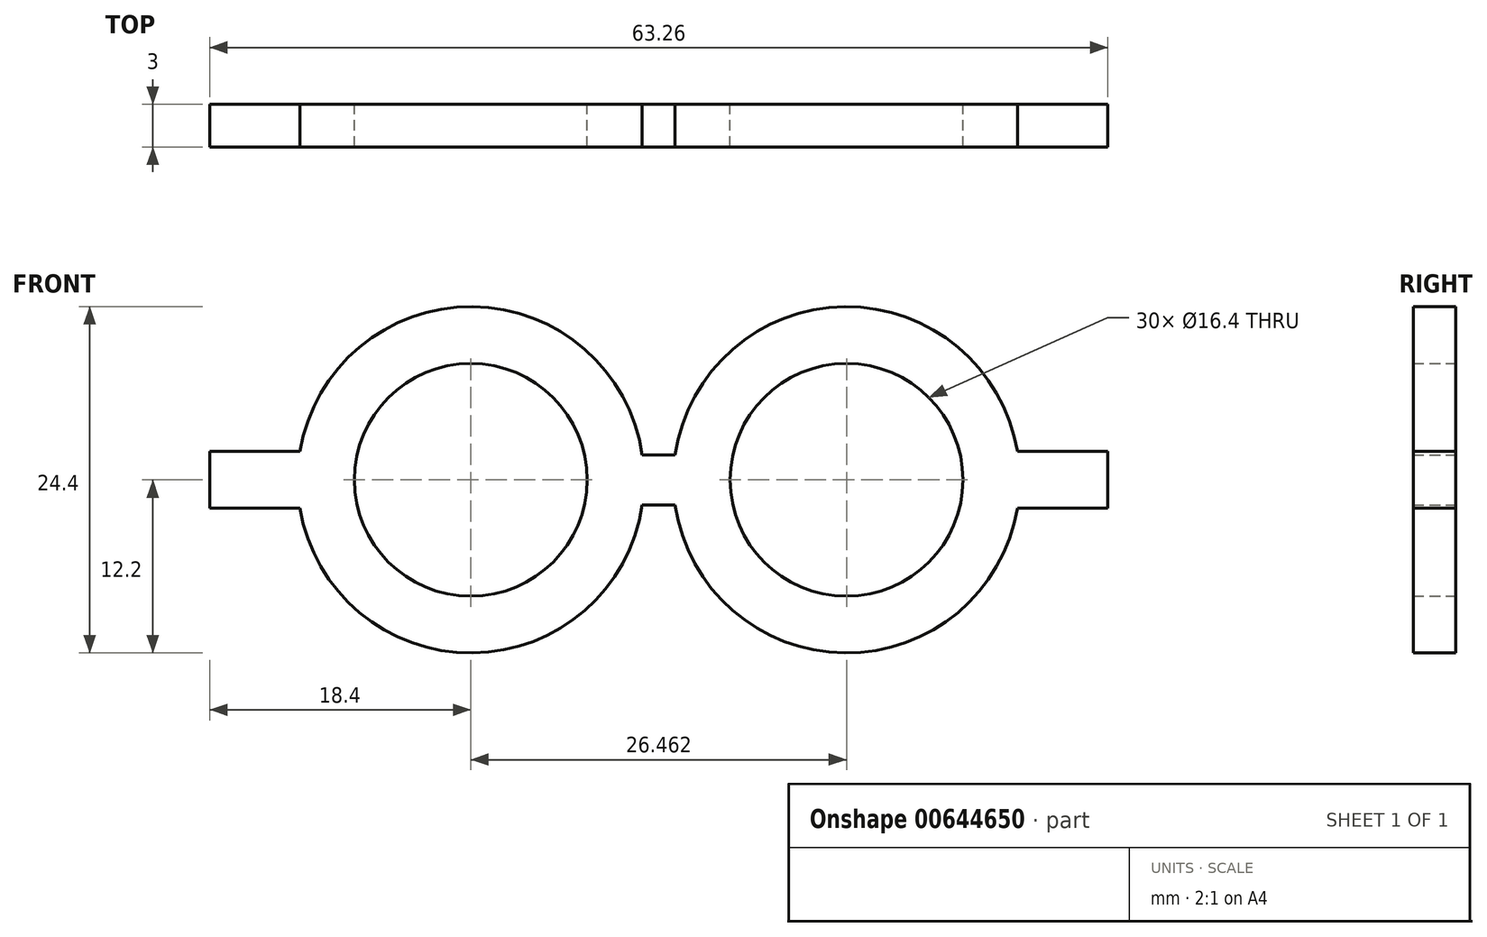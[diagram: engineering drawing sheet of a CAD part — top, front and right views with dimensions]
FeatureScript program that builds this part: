
annotation { "Feature Type Name" : "Feature", "Feature Type Description" : "" }
export const myFeature = defineFeature(function(context is Context, id is Id, definition is map)
    precondition{}
    {
        {
            var Q0;
            Q0=qCreatedBy(makeId("Front.planeOp"),FACE);
            var sketch = newSketch(context, id + "F0", { "sketchPlane" : qUnion([Q0])});
            skCircle(sketch, "E0", {"center": v(0, 0) * mm, "radius": 8.2 * mm});
            skCircle(sketch, "E1", {"center": v(26.46, 0) * mm, "radius": 8.2 * mm});
            skArc(sketch, "E2.0", {"start": v(-12.03, -2) * mm, "mid": v(12.2, 0) * mm, "end": v(-12.03, 2) * mm});
            skArc(sketch, "E3.0", {"start": v(38.5, 2) * mm, "mid": v(14.26, 0) * mm, "end": v(38.5, -2) * mm});
            skLineSegment(sketch, "E4.bottom", {"start": v(12.07, 1.76) * mm, "end": v(14.39, 1.76) * mm});
            skLineSegment(sketch, "E4.top", {"start": v(12.07, -1.76) * mm, "end": v(14.39, -1.76) * mm});
            skPoint(sketch, "E4.middle", {"position": v(13.25, 0) * mm});
            skLineSegment(sketch, "E5.right", {"start": v(44.86, 2) * mm, "end": v(44.86, -2) * mm});
            skPoint(sketch, "E5.middle", {"position": v(35.66, 0) * mm});
            skLineSegment(sketch, "E6.bottom", {"start": v(-7.95, 2) * mm, "end": v(-18.4, 2) * mm});
            skLineSegment(sketch, "E6.top", {"start": v(-7.95, -2) * mm, "end": v(-18.4, -2) * mm});
            skLineSegment(sketch, "E6.right", {"start": v(-18.4, 2) * mm, "end": v(-18.4, -2) * mm});
            skPoint(sketch, "E6.middle", {"position": v(-9.2, 0) * mm});
            skLineSegment(sketch, "E7.trimOffspring", {"start": v(38.5, 2) * mm, "end": v(44.86, 2) * mm});
            skLineSegment(sketch, "E8.trimOffspring", {"start": v(38.5, -2) * mm, "end": v(44.86, -2) * mm});
            skPoint(sketch, "E5.bottom.start.orphan", {"position": v(26.46, 2) * mm});
            skPoint(sketch, "E5.top.start.orphan", {"position": v(26.46, -2) * mm});
            skPoint(sketch, "E9.orphan", {"position": v(0, 2) * mm});
            skPoint(sketch, "E6.left.end.orphan", {"position": v(0, -2) * mm});
            skPoint(sketch, "E4.right.start.orphan", {"position": v(16.75, 1.76) * mm});
            skPoint(sketch, "E10.orphan", {"position": v(16.75, -1.76) * mm});
            skPoint(sketch, "E11.orphan", {"position": v(9.75, 1.76) * mm});
            skPoint(sketch, "E12.orphan", {"position": v(9.75, -1.76) * mm});
            skSolve(sketch);
        }
        {
            var Q0;
            Q0 = qSketchRegion(id + "F0", true);
            extrude(context, id + "F1", {"entities" : qUnion([Q0]), "depth" : 3 * mm, "offsetDistance" : 25 * mm});
        }
    });
